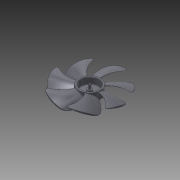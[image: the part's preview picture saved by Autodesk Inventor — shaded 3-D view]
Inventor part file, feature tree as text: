
AUTODESK INVENTOR PART (.ipt)
format: ipt  version: 2011 SP2 (Build 150309200, 309)  size: 1,059,328 bytes
history: native  units: mm
features: sketch x7, fillet x3, revolve x3, plane x2, extrude x2, loft x1, pattern_circular x1, chamfer x1
ambient origin geometry x8: Origin, YZ Plane, XZ Plane, XY Plane, X Axis, Y Axis, Z Axis, Center Point
bodies: Solid1 (feature_tree), Solid2 (feature_tree)
feature tree (20):
  sketch  "Sketch1"  dims[d0=10.0mm d1=15.0deg]
  plane  "Work Plane1"
  plane  "Work Plane2"
  loft  "Loft1"
  extrude  "Extrusion1"  TaperAngle=90.0deg  [1 undecoded]
  fillet  "Fillet1"  Radius=15.0mm
  pattern_circular  "Circular Pattern1"  Count=20  [1 undecoded]
  extrude  "Extrusion2"  Depth=100.0mm
  revolve  "Revolution1"  Angle=90.0deg
  fillet  "Fillet2"  [1 undecoded]
  fillet  "Fillet3"  [1 undecoded]
  sketch  "Sketch7"  dims[d11=15.0deg d12=100.0mm d13=0.0mm d14=90.0deg d15=0.0mm d16=90.0deg d17=0.0mm d18=90.0deg d19=45.0mm d23=2.0mm d24=12.0mm d25=45.0deg d26=10.0mm d27=0.0mm d28=0.5mm d29=0.0mm d30=0.5mm d31=0.0mm d32=70.0mm d33=360.0deg d35=15.0mm d36=6.0mm d37=5.5mm d38=0.0mm d39=0.0mm d40=3.25mm d41=2.5mm d42=12.5mm d43=6.0mm d44=90.0deg d45=0.5mm d46=0.5mm d47=1.5mm d48=0.5mm d49=1.0mm d51=2.0mm d52=0.5mm d53=0.75mm d54=2.0mm d55=11.0mm d56=2.0mm d57=8.0mm d58=90.0deg d59=90.0deg d60=0.5mm d61=2.0mm d62=45.0deg]
  revolve  "Revolution2"  [1 undecoded]
  revolve  "Revolution3"  [1 undecoded]
  chamfer  "Chamfer1"  Distance=12.0mm
  sketch  "Sketch2"  dims[d2=45.0mm d3=90.0deg d4=15.0mm]
  sketch  "Sketch3"  dims[d5=45.0deg]
  sketch  "Sketch4"  dims[d6=10.0mm]
  sketch  "Sketch5"  dims[d7=45.0mm]
  sketch  "Sketch6"  dims[d8=45.0mm d9=200.0mm]
note: 6 required parameter values undecoded (feature->parameter linkage not recoverable at this tier; creation-order binding heuristic only, values carry confidence <= 0.55)